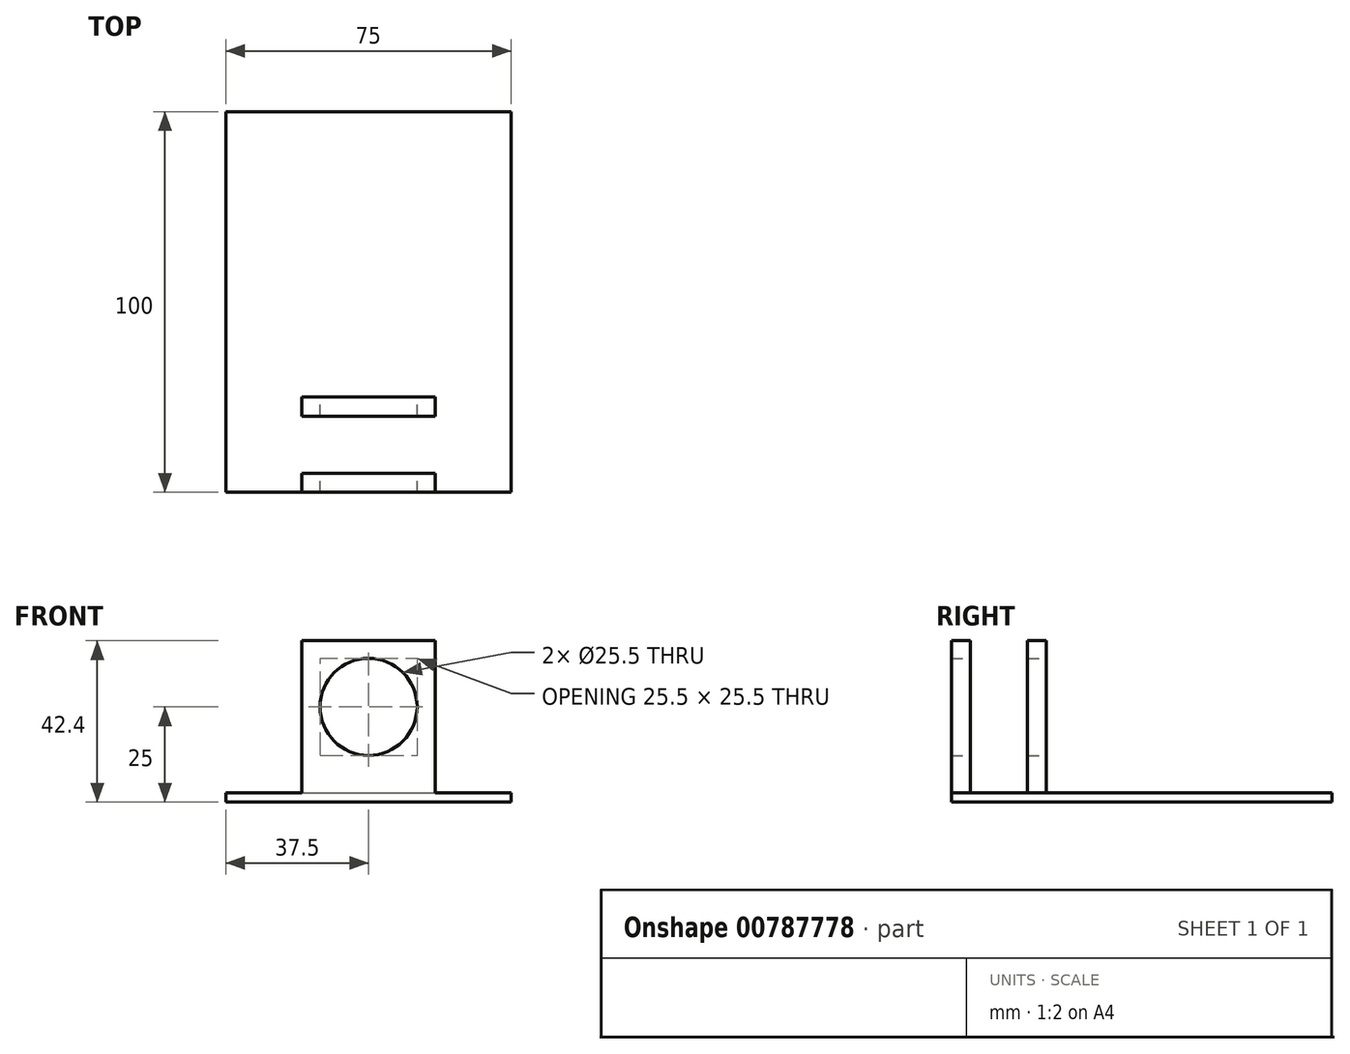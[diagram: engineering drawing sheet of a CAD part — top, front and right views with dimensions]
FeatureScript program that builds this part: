
annotation { "Feature Type Name" : "Feature", "Feature Type Description" : "" }
export const myFeature = defineFeature(function(context is Context, id is Id, definition is map)
    precondition{}
    {
        {
            var Q0;
            Q0=qCreatedBy(makeId("Front.planeOp"),FACE);
            var sketch = newSketch(context, id + "F0", { "sketchPlane" : qUnion([Q0])});
            skLineSegment(sketch, "E0.bottom", {"start": v(-37.5, 0) * mm, "end": v(37.5, 0) * mm});
            skLineSegment(sketch, "E0.top", {"start": v(-37.5, -2.4) * mm, "end": v(37.5, -2.4) * mm});
            skLineSegment(sketch, "E0.left", {"start": v(-37.5, 0) * mm, "end": v(-37.5, -2.4) * mm});
            skLineSegment(sketch, "E0.right", {"start": v(37.5, 0) * mm, "end": v(37.5, -2.4) * mm});
            skLineSegment(sketch, "E1.bottom", {"start": v(-17.5, 0) * mm, "end": v(17.5, 0) * mm});
            skLineSegment(sketch, "E1.top", {"start": v(-17.5, 40) * mm, "end": v(17.5, 40) * mm});
            skLineSegment(sketch, "E1.left", {"start": v(-17.5, 0) * mm, "end": v(-17.5, 40) * mm});
            skLineSegment(sketch, "E1.right", {"start": v(17.5, 0) * mm, "end": v(17.5, 40) * mm});
            skCircle(sketch, "E2", {"center": v(0, 22.6) * mm, "radius": 12.75 * mm});
            skSolve(sketch);
        }
        {
            var Q0;
            Q0=makeQuery(id+"F0.imprint","IMPRINT",FACE,{"disambiguationData":[TD([[makeQuery(id+"F0.imprint","IMPRINT",EDGE,{"derivedFrom":sQuery(id+"F0.wireOp",EDGE,"E1.top")}),-1.0]])]});
            var Q1;
            Q1=makeQuery(id+"F0.imprint","IMPRINT",FACE,{"disambiguationData":[TD([[makeQuery(id+"F0.imprint","IMPRINT",EDGE,{"derivedFrom":sQuery(id+"F0.wireOp",EDGE,"E0.top")}),1.0]])]});
            extrude(context, id + "F1", {"entities" : qUnion([Q0, Q1]), "depth" : 100 * mm, "offsetDistance" : 25 * mm});
        }
        {
            var Q0;
            Q0=qCreatedBy(makeId("Right.planeOp"),FACE);
            var sketch = newSketch(context, id + "F2", { "sketchPlane" : qUnion([Q0])});
            skLineSegment(sketch, "E3.bottom", {"start": v(-95, 0) * mm, "end": v(-80, 0) * mm});
            skLineSegment(sketch, "E3.top", {"start": v(-95, 40) * mm, "end": v(-80, 40) * mm});
            skLineSegment(sketch, "E3.left", {"start": v(-95, 0) * mm, "end": v(-95, 40) * mm});
            skLineSegment(sketch, "E3.right", {"start": v(-80, 0) * mm, "end": v(-80, 40) * mm});
            skLineSegment(sketch, "E4.bottom", {"start": v(-75, 40) * mm, "end": v(0, 40) * mm});
            skLineSegment(sketch, "E4.top", {"start": v(-75, 0) * mm, "end": v(0, 0) * mm});
            skLineSegment(sketch, "E4.left", {"start": v(-75, 40) * mm, "end": v(-75, 0) * mm});
            skLineSegment(sketch, "E4.right", {"start": v(0, 40) * mm, "end": v(0, 0) * mm});
            skSolve(sketch);
        }
        {
            var Q0;
            Q0=makeQuery(id+"F2.imprint","IMPRINT",FACE,{"disambiguationData":[TD([[makeQuery(id+"F2.imprint","IMPRINT",EDGE,{"derivedFrom":sQuery(id+"F2.wireOp",EDGE,"E3.bottom")}),1.0]])]});
            var Q1;
            Q1=makeQuery(id+"F2.imprint","IMPRINT",FACE,{"disambiguationData":[TD([[makeQuery(id+"F2.imprint","IMPRINT",EDGE,{"derivedFrom":sQuery(id+"F2.wireOp",EDGE,"E4.bottom")}),-1.0]])]});
            extrude(context, id + "F3", {"entities" : qUnion([Q0, Q1]), "operationType" : NewBodyOperationType.REMOVE, "endBound" : BoundingType.SYMMETRIC, "oppositeDirection" : true, "depth" : 45 * mm, "offsetDistance" : 25 * mm});
        }
    });
